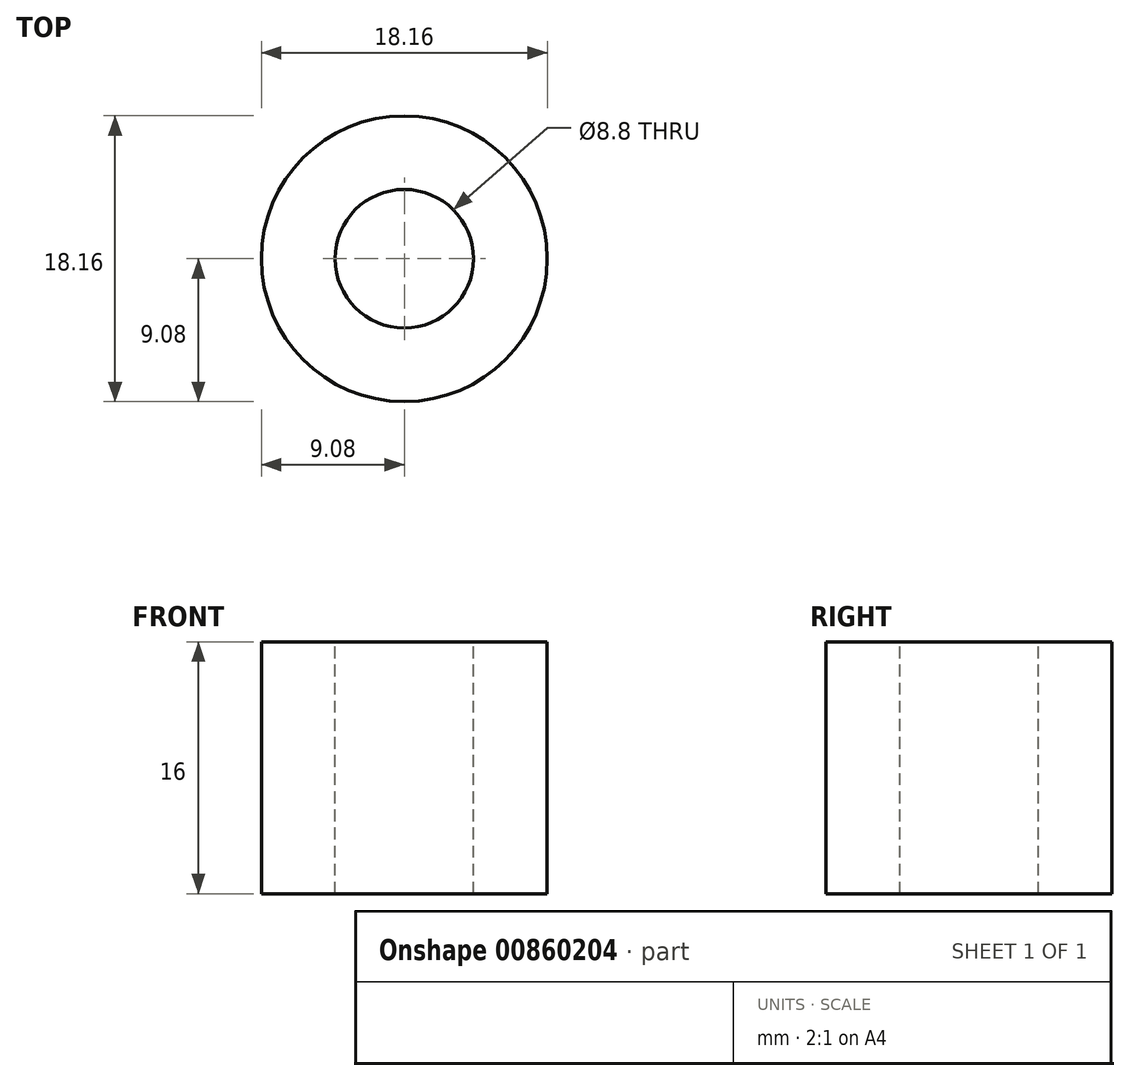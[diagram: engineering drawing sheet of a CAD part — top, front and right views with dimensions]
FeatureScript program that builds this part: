
annotation { "Feature Type Name" : "Feature", "Feature Type Description" : "" }
export const myFeature = defineFeature(function(context is Context, id is Id, definition is map)
    precondition{}
    {
        {
            var Q0;
            Q0=qCreatedBy(makeId("Top.planeOp"),FACE);
            var sketch = newSketch(context, id + "F0", { "sketchPlane" : qUnion([Q0])});
            skCircle(sketch, "E0", {"center": v(0, 0) * mm, "radius": 9.07 * mm});
            skSolve(sketch);
        }
        {
            var Q0;
            Q0=makeQuery(id+"F0.imprint","IMPRINT",FACE,{"disambiguationData":[TD([[makeQuery(id+"F0.imprint","IMPRINT",EDGE,{"derivedFrom":sQuery(id+"F0.wireOp",EDGE,"E0")}),1.0]])]});
            extrude(context, id + "F1", {"entities" : qUnion([Q0]), "oppositeDirection" : true, "depth" : 16 * mm, "offsetDistance" : 25 * mm});
        }
        {
            var Q0;
            Q0=sQuery(id+"F0.wireOp",VERTEX,"E0.center");
            var Q1;
            Q1=makeQuery(id+"F1.opExtrude","SWEPT_BODY",BODY,{"disambiguationData":[OSD([sQuery(id+"F0.wireOp",EDGE,"E0")])]});
            hole(context, id + "F2", {"style" : HoleStyle.SIMPLE, "endStyle" : HoleEndStyle.THROUGH, "standardTappedOrClearance" : lookupTablePath({ "fit" : "Normal", "standard" : "ISO", "size" : "M8", "type" : "Clearance" }), "standardBlindInLast" : lookupTablePath({ "fit" : "Standard", "standard" : "ISO", "size" : "M8", "type" : "Clearance" }), "holeDiameter" : 8.8 * mm, "majorDiameter" : 5 * mm, "isTappedThrough" : true, "tappedDepth" : 12.7 * mm, "tapClearance" : 3, "locations" : qUnion([Q0]), "scope" : qUnion([Q1])});
        }
    });
